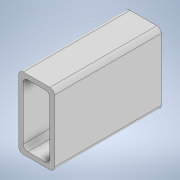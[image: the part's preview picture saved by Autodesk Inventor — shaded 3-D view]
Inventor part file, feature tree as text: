
AUTODESK INVENTOR PART (.ipt)
format: ipt  version: 2020 (Build 240168000, 168)  size: 117,248 bytes
history: native  units: in
note: dims shown in document units (in); Inventor stores cm internally (conversion verified against a paired STEP export)
features: extrude x1, sketch x1
ambient origin geometry x8: Origin, YZ Plane, XZ Plane, XY Plane, X Axis, Y Axis, Z Axis, Center Point
bodies: Solid1 (feature_tree)
feature tree (2):
  extrude  "Extrusion1"  Depth=1.0in
  sketch  "Sketch1"  dims[d0=2.0in d1=1.0in d2=0.125in d3=0.125in d4=0.125in d5=0.125in d6=0.125in d7=0.125in d8=0.125in d9=0.125in d10=0.125in d11=3.0in d12=0.0in]
